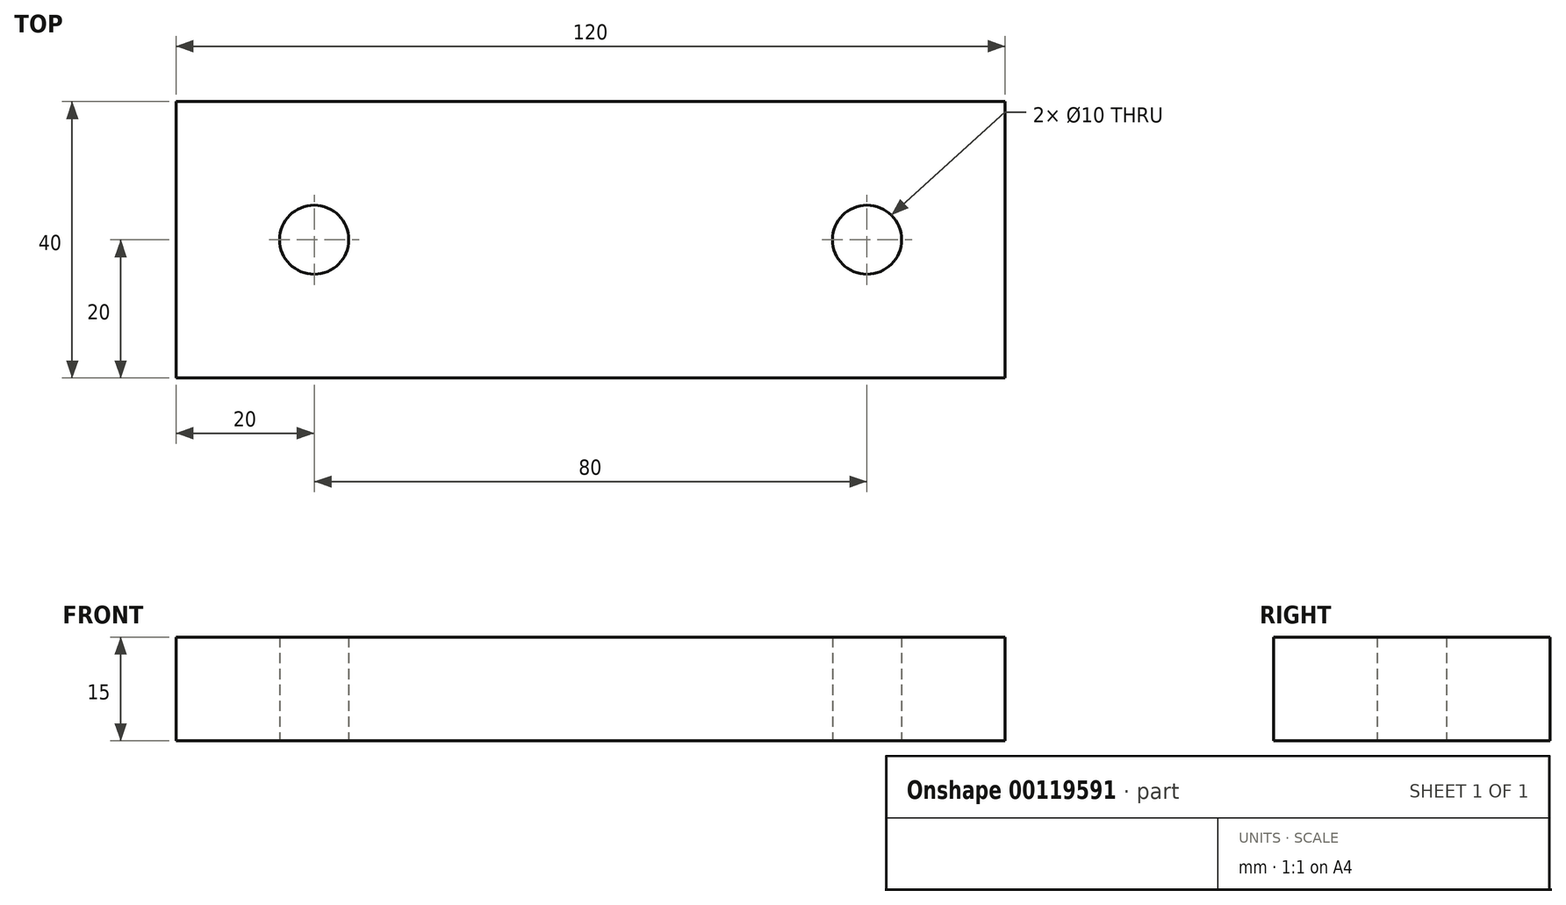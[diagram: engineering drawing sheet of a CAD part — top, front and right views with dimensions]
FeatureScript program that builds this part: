
annotation { "Feature Type Name" : "Feature", "Feature Type Description" : "" }
export const myFeature = defineFeature(function(context is Context, id is Id, definition is map)
    precondition{}
    {
        {
            var Q0;
            Q0=qCreatedBy(makeId("Top.planeOp"),FACE);
            var sketch = newSketch(context, id + "F0", { "sketchPlane" : qUnion([Q0])});
            skLineSegment(sketch, "E0.bottom", {"start": v(0, 0) * mm, "end": v(120, 0) * mm});
            skLineSegment(sketch, "E0.top", {"start": v(0, 40) * mm, "end": v(120, 40) * mm});
            skLineSegment(sketch, "E0.left", {"start": v(0, 0) * mm, "end": v(0, 40) * mm});
            skLineSegment(sketch, "E0.right", {"start": v(120, 0) * mm, "end": v(120, 40) * mm});
            skCircle(sketch, "E1", {"center": v(20, 20) * mm, "radius": 5 * mm});
            skCircle(sketch, "E2", {"center": v(100, 20) * mm, "radius": 5 * mm});
            skSolve(sketch);
        }
        {
            var Q0;
            Q0=makeQuery(id+"F0.imprint","IMPRINT",FACE,{"disambiguationData":[TD([[makeQuery(id+"F0.imprint","IMPRINT",EDGE,{"derivedFrom":sQuery(id+"F0.wireOp",EDGE,"E0.bottom")}),1.0]])]});
            extrude(context, id + "F1", {"entities" : qUnion([Q0]), "depth" : 15 * mm});
        }
    });
